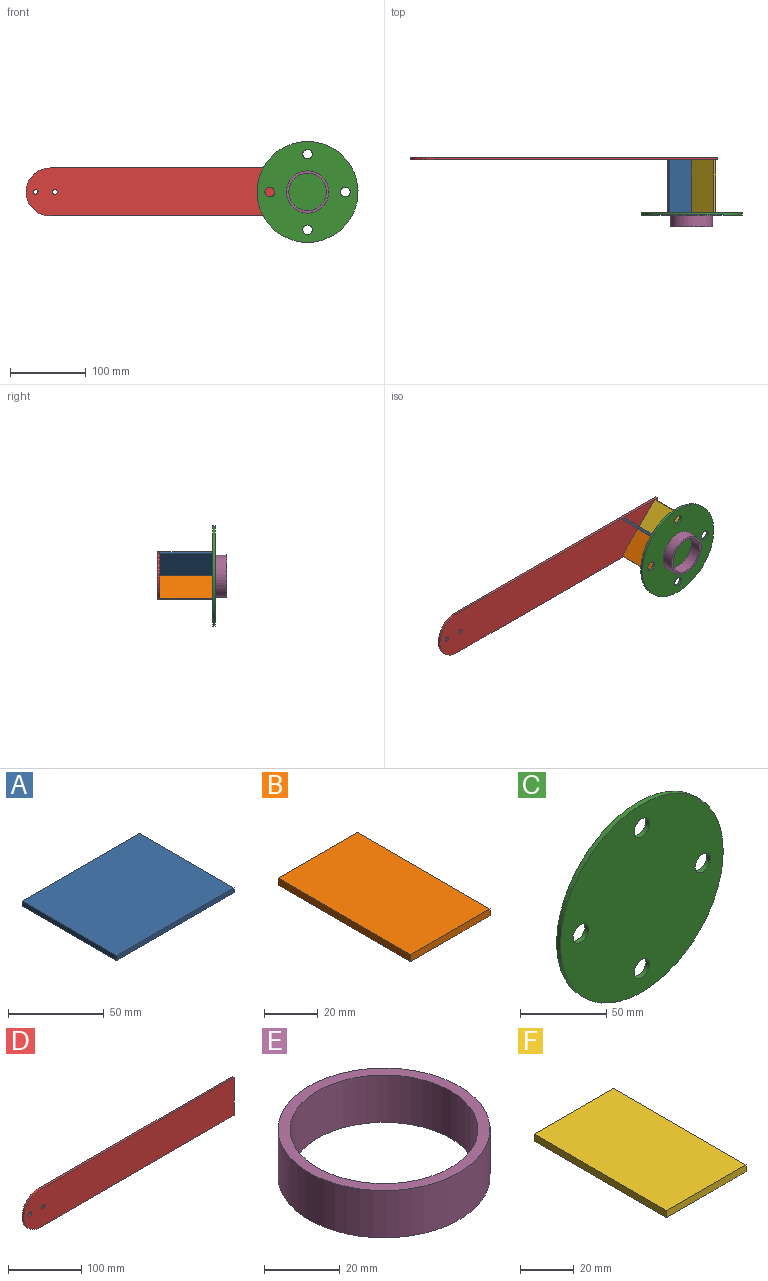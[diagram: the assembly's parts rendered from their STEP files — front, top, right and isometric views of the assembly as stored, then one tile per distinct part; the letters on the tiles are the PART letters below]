
ASSEMBLY  parts=6 mates=5
PART A: 6 faces, bbox 86.6x69.9x3.2 mm
  f0: plane 86.61x3.18mm, normal (0,1,0), area 275mm2, adj f1,f3,f4,f5
  f1: plane 69.85x3.18mm, normal (-1,0,0), area 221.8mm2, adj f0,f2,f4,f5
  f2: plane 86.61x3.18mm, normal (0,-1,0), area 275mm2, adj f1,f3,f4,f5
  f3: plane 69.85x3.18mm, normal (1,0,0), area 221.8mm2, adj f0,f2,f4,f5
  f4: plane 86.61x69.85mm, normal (0,0,1), area 6050mm2, adj f0,f1,f2,f3
  f5: plane 86.61x69.85mm, normal (0,0,-1), area 6050mm2, adj f0,f1,f2,f3
PART B: 6 faces, bbox 41.7x69.9x3.2 mm
  f0: plane 69.85x3.18mm, normal (1,0,0), area 221.8mm2, adj f1,f3,f4,f5
  f1: plane 41.73x3.18mm, normal (0,1,0), area 132.5mm2, adj f0,f2,f4,f5
  f2: plane 69.85x3.18mm, normal (-1,0,0), area 221.8mm2, adj f1,f3,f4,f5
  f3: plane 41.73x3.18mm, normal (0,-1,0), area 132.5mm2, adj f0,f2,f4,f5
  f4: plane 69.85x41.73mm, normal (0,0,1), area 2915mm2, adj f0,f1,f2,f3
  f5: plane 69.85x41.73mm, normal (0,0,-1), area 2915mm2, adj f0,f1,f2,f3
PART C: 7 faces, bbox 133.4x3.2x133.4 mm
  f0: cylinder r=6.35mm len=12.7mm, axis (0,1,0), area 126.7mm2, adj f5,f6
  f1: cylinder r=6.35mm len=12.7mm, axis (0,1,0), area 126.7mm2, adj f5,f6
  f2: cylinder r=66.67mm len=133.35mm, axis (0,1,0), area 1330.1mm2, adj f5,f6
  f3: cylinder r=6.35mm len=12.7mm, axis (0,1,0), area 126.7mm2, adj f5,f6
  f4: cylinder r=6.35mm len=12.7mm, axis (0,1,0), area 126.7mm2, adj f5,f6
  f5: plane 133.35x133.35mm, normal (0,-1,0), area 13459.4mm2, adj f0,f1,f2,f3,f4
  f6: plane 133.35x133.35mm, normal (0,1,0), area 13459.4mm2, adj f0,f1,f2,f3,f4
PART D: 8 faces, bbox 406.4x3.2x63.5 mm
  f0: plane 374.65x3.18mm, normal (0,0,1), area 1189.5mm2, adj f1,f4,f6,f7
  f1: cylinder r=31.75mm len=63.5mm, axis (0,1,0), area 316.7mm2, adj f0,f2,f6,f7
  f2: plane 374.65x3.18mm, normal (0,0,-1), area 1189.5mm2, adj f1,f4,f6,f7
  f3: cylinder r=3.17mm len=6.35mm, axis (0,1,0), area 63.3mm2, adj f6,f7
  f4: plane 63.5x3.18mm, normal (1,0,0), area 201.6mm2, adj f0,f2,f6,f7
  f5: cylinder r=3.17mm len=6.35mm, axis (0,1,0), area 63.3mm2, adj f6,f7
  f6: plane 406.4x63.5mm, normal (0,-1,0), area 25310.4mm2, adj f0,f1,f2,f3,f4,f5
  f7: plane 406.4x63.5mm, normal (0,1,0), area 25310.4mm2, adj f0,f1,f2,f3,f4,f5
PART E: 4 faces, bbox 55.9x55.9x15.2 mm
  f0: cylinder r=24.77mm len=49.53mm, axis (0,0,-1), area 2371.4mm2, adj f2,f3
  f1: cylinder r=27.94mm len=55.88mm, axis (0,0,-1), area 2675.4mm2, adj f2,f3
  f2: plane 55.88x55.88mm, normal (0,0,1), area 525.7mm2, adj f0,f1
  f3: plane 55.88x55.88mm, normal (0,0,-1), area 525.7mm2, adj f0,f1
PART F: 6 faces, bbox 41.7x69.9x3.2 mm
  f0: plane 69.85x3.18mm, normal (1,0,0), area 221.8mm2, adj f1,f3,f4,f5
  f1: plane 41.73x3.18mm, normal (0,1,0), area 132.5mm2, adj f0,f2,f4,f5
  f2: plane 69.85x3.18mm, normal (-1,0,0), area 221.8mm2, adj f1,f3,f4,f5
  f3: plane 41.73x3.18mm, normal (0,-1,0), area 132.5mm2, adj f0,f2,f4,f5
  f4: plane 69.85x41.73mm, normal (0,0,1), area 2915mm2, adj f0,f1,f2,f3
  f5: plane 69.85x41.73mm, normal (0,0,-1), area 2915mm2, adj f0,f1,f2,f3
PLACE A rot(axis=(-0.92,0,0.38),180deg) t=(213.68,71.52,83.87)mm
PLACE B rot(axis=(-0.92,0,-0.38),180deg) t=(245.43,71.52,56.61)mm
PLACE C rot(axis=(0,1,0),90deg) t=(243.18,1.67,52.12)mm
PLACE D t=(-128.91,74.7,20.37)mm
PLACE E rot(axis=(-0.58,0.58,0.58),120deg) t=(243.18,-16.74,52.12)mm
PLACE F rot(axis=(-0.38,0,0.92),180deg) t=(240.94,-11.03,47.63)mm
MATE fastened F.f0 <-> A.f5  axis (-0.71,0,-0.71) through (244.31,36.6,53.24)mm
MATE revolute A.f0 <-> C.f2  axis (0,-1,0) through (243.18,1.67,52.12)mm
MATE fastened E.f0 <-> C.f2  axis (0,-1,0) through (243.18,-1.5,52.12)mm
MATE revolute A.f2 <-> D.f6  axis (0,1,0) through (243.18,71.52,52.12)mm
MATE fastened B.f0 <-> A.f4  axis (0.71,0,0.71) through (242.06,36.6,51)mm
